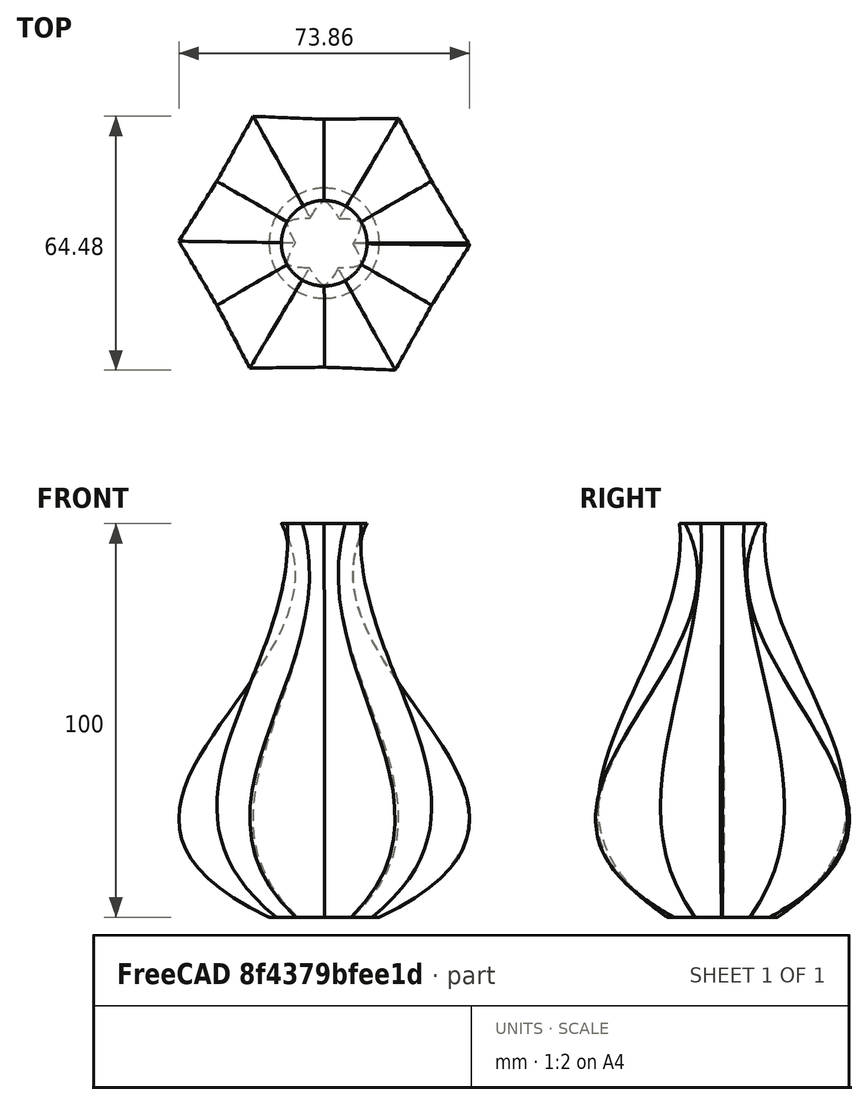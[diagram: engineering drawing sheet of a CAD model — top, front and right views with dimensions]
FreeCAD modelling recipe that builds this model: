
FCSTD DOCUMENT  (FreeCAD 0.21R33771 (Git))
Label: vase_loft
License: All rights reserved
LicenseURL: https://en.wikipedia.org/wiki/All_rights_reserved
objects: Sketcher::SketchObject×4, PartDesign::Body×1, Part::Loft×1
note: 6 computed .brp shape members not serialized (recipe doc carries the construction recipe); baked Part::Feature solids carry a one-line shape summary decoded from their .brp

FEATURE [Sketcher::SketchObject] Sketch
  FullyConstrained = false
  MapMode = 5
  Support = -> [XY_Plane]
  sketch-geometry (1):
    g0: Circle CenterX=0 CenterY=0 CenterZ=0 NormalX=0 NormalY=0 NormalZ=1 AngleXU=0 Radius=14.0029
  constraints (1):
    c: Coincident(g0,g-1)
FEATURE [Sketcher::SketchObject] Sketch001
  AttachmentOffset = pos=(0,0,30) rot=(0,0,1;0rad)
  FullyConstrained = false
  MapMode = 5
  Placement = pos=(0,0,30) rot=(0,0,1;0rad)
  Support = -> [XY_Plane]
  sketch-geometry (7):
    g0: LineSegment StartX=17.7205 StartY=-31.6972 StartZ=0 EndX=36.3108 EndY=-0.502213 EndZ=0
    g1: LineSegment StartX=36.3108 StartY=-0.502213 StartZ=0 EndX=18.5903 EndY=31.195 EndZ=0
    g2: LineSegment StartX=18.5903 StartY=31.195 StartZ=0 EndX=-17.7205 EndY=31.6972 EndZ=0
    g3: LineSegment StartX=-17.7205 StartY=31.6972 StartZ=0 EndX=-36.3108 EndY=0.502213 EndZ=0
    g4: LineSegment StartX=-36.3108 StartY=0.502213 StartZ=0 EndX=-18.5903 EndY=-31.195 EndZ=0
    g5: LineSegment StartX=-18.5903 StartY=-31.195 StartZ=0 EndX=17.7205 EndY=-31.6972 EndZ=0
    g6: Circle CenterX=0 CenterY=0 CenterZ=0 NormalX=0 NormalY=0 NormalZ=1 AngleXU=0 Radius=36.3143
  constraints (14):
    c: Coincident(g0,g1)
    c: Coincident(g1,g2)
    c: Coincident(g2,g3)
    c: Coincident(g3,g4)
    c: Coincident(g4,g5)
    c: Coincident(g5,g0)
    c: Equal(g0, g1-g5) x5
    c: PointOnObject(g0,g6)
    c: PointOnObject(g1,g6)
    c: PointOnObject(g2,g6)
    c: PointOnObject(g3,g6)
    c: PointOnObject(g4,g6)
    c: PointOnObject(g5,g6)
    c: Coincident(g6,g-1)
FEATURE [Sketcher::SketchObject] Sketch002
  AttachmentOffset = pos=(0,0,60) rot=(0,0,1;0rad)
  FullyConstrained = false
  MapMode = 5
  Placement = pos=(0,0,60) rot=(0,0,1;0rad)
  Support = -> [XY_Plane]
  sketch-geometry (7):
    g0: LineSegment StartX=0.0188403 StartY=-21.4448 StartZ=0 EndX=18.5812 EndY=-10.7061 EndZ=0
    g1: LineSegment StartX=18.5812 StartY=-10.7061 StartZ=0 EndX=18.5623 EndY=10.7387 EndZ=0
    g2: LineSegment StartX=18.5623 StartY=10.7387 StartZ=0 EndX=-0.0188403 EndY=21.4448 EndZ=0
    g3: LineSegment StartX=-0.0188403 StartY=21.4448 StartZ=0 EndX=-18.5812 EndY=10.7061 EndZ=0
    g4: LineSegment StartX=-18.5812 StartY=10.7061 StartZ=0 EndX=-18.5623 EndY=-10.7387 EndZ=0
    g5: LineSegment StartX=-18.5623 StartY=-10.7387 StartZ=0 EndX=0.0188403 EndY=-21.4448 EndZ=0
    g6: Circle CenterX=0 CenterY=0 CenterZ=0 NormalX=0 NormalY=0 NormalZ=1 AngleXU=0 Radius=21.4448
  constraints (14):
    c: Coincident(g0,g1)
    c: Coincident(g1,g2)
    c: Coincident(g2,g3)
    c: Coincident(g3,g4)
    c: Coincident(g4,g5)
    c: Coincident(g5,g0)
    c: Equal(g0, g1-g5) x5
    c: PointOnObject(g0,g6)
    c: PointOnObject(g1,g6)
    c: PointOnObject(g2,g6)
    c: PointOnObject(g3,g6)
    c: PointOnObject(g4,g6)
    c: PointOnObject(g5,g6)
    c: Coincident(g6,g-1)
FEATURE [Sketcher::SketchObject] Sketch003
  AttachmentOffset = pos=(0,0,100) rot=(0,0,1;0rad)
  FullyConstrained = false
  MapMode = 5
  Placement = pos=(0,0,100) rot=(0,0,1;0rad)
  Support = -> [XY_Plane]
  sketch-geometry (1):
    g0: Circle CenterX=0 CenterY=0 CenterZ=0 NormalX=0 NormalY=0 NormalZ=1 AngleXU=0 Radius=10.8734
  constraints (1):
    c: Coincident(g0,g-1)
FEATURE [PartDesign::Body] Body
  Group = -> [Sketch,Sketch001,Sketch002,Sketch003]
  Origin = -> Origin
FEATURE [Part::Loft] Loft
  Closed = false
  MaxDegree = 5
  Ruled = false
  Sections = -> [Sketch,Sketch001,Sketch002,Sketch003]
  Solid = true
